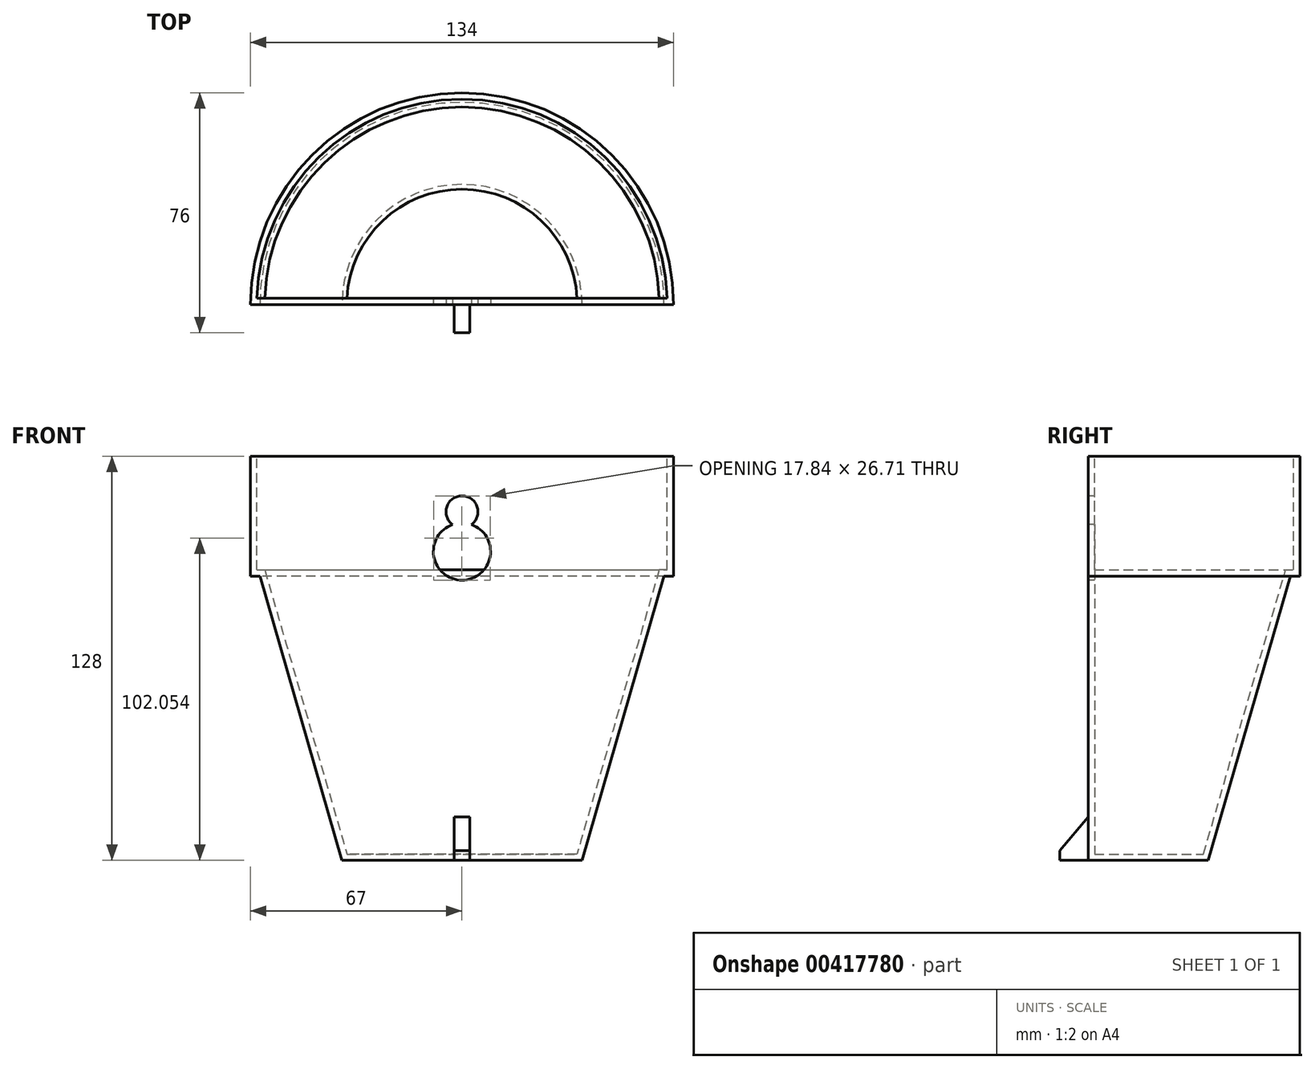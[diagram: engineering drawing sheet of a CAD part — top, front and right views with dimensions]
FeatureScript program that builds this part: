
annotation { "Feature Type Name" : "Feature", "Feature Type Description" : "" }
export const myFeature = defineFeature(function(context is Context, id is Id, definition is map)
    precondition{}
    {
        {
            var Q0;
            Q0=qCreatedBy(makeId("Front.planeOp"),FACE);
            var sketch = newSketch(context, id + "F0", { "sketchPlane" : qUnion([Q0])});
            skLineSegment(sketch, "E0", {"start": v(0, 56.42) * mm, "end": v(-67, 56.42) * mm});
            skLineSegment(sketch, "E1", {"start": v(-67, 56.42) * mm, "end": v(-67, 18.42) * mm});
            skLineSegment(sketch, "E2", {"start": v(0, -71.58) * mm, "end": v(-38, -71.58) * mm});
            skLineSegment(sketch, "E3", {"start": v(-67, 18.42) * mm, "end": v(-64, 18.42) * mm});
            skLineSegment(sketch, "E4", {"start": v(0, 56.42) * mm, "end": v(0, -71.58) * mm});
            skLineSegment(sketch, "E5", {"start": v(-64, 18.42) * mm, "end": v(-38, -71.58) * mm});
            skLineSegment(sketch, "E6.MirrorCS", {"start": v(0, 56.42) * mm, "end": v(67, 56.42) * mm});
            skLineSegment(sketch, "E7.MirrorCS", {"start": v(67, 56.42) * mm, "end": v(67, 18.42) * mm});
            skLineSegment(sketch, "E8.MirrorCS", {"start": v(67, 18.42) * mm, "end": v(64, 18.42) * mm});
            skLineSegment(sketch, "E9.MirrorCS", {"start": v(64, 18.42) * mm, "end": v(38, -71.58) * mm});
            skLineSegment(sketch, "E10.MirrorCS", {"start": v(0, -71.58) * mm, "end": v(38, -71.58) * mm});
            skSolve(sketch);
        }
        {
            var Q0;
            {var subQ0=sQuery(id+"F0.wireOp",EDGE,"E3");Q0=makeQuery(id+"F0.imprint","IMPRINT",FACE,{"disambiguationData":[TD([[makeQuery(id+"F0.imprint","IMPRINT",EDGE,{"derivedFrom":subQ0}),1.0]])]});}
            var Q1;
            {var subQ1=sQuery(id+"F0.wireOp",EDGE,"E0");Q1=makeQuery(id+"F0.imprint","IMPRINT",FACE,{"disambiguationData":[TD([[makeQuery(id+"F0.imprint","IMPRINT",EDGE,{"derivedFrom":subQ1}),1.0]])]});}
            var Q2;
            Q2=makeQuery(id+"F0.imprint","IMPRINT",FACE,{"disambiguationData":[TD([[makeQuery(id+"F0.imprint","IMPRINT",EDGE,{"derivedFrom":sQuery(id+"F0.wireOp",EDGE,"Kfnrekvc-ZjTY-c2iQ-cK4z-hKnBe4uEAVNk")}),1.0]])]});
            var Q3;
            Q3=sQuery(id+"F0.wireOp",EDGE,"E4");
            revolve(context, id + "F1", {"entities" : qUnion([Q0, Q1, Q2]), "axis" : qUnion([Q3]), "revolveType" : RevolveType.ONE_DIRECTION, "angle" : 180 * degree});
        }
        {
            var Q0;
            Q0=makeQuery(id+"FK2OT3XlAi37Aaq_1.splitOp","SPLIT",FACE,{"derivedFrom":makeQuery(id+"F1.opRevolve","SWEPT_FACE",FACE,{"disambiguationData":[OSD([sQuery(id+"F0.wireOp",EDGE,"E0")])]}),"isFromBackBody":true});
            shell(context, id + "F2", {"entities" : qUnion([Q0]), "thickness" : 2 * mm});
        }
        {
            var Q0;
            Q0=qCreatedBy(makeId("Front.planeOp"),FACE);
            var sketch = newSketch(context, id + "F3", { "sketchPlane" : qUnion([Q0])});
            skLineSegment(sketch, "E11.bottom", {"start": v(-2.5, -56.58) * mm, "end": v(2.5, -56.58) * mm});
            skLineSegment(sketch, "E11.top", {"start": v(-2.5, -71.58) * mm, "end": v(2.5, -71.58) * mm});
            skLineSegment(sketch, "E11.left", {"start": v(-2.5, -56.58) * mm, "end": v(-2.5, -71.58) * mm});
            skLineSegment(sketch, "E11.right", {"start": v(2.5, -56.58) * mm, "end": v(2.5, -71.58) * mm});
            skPoint(sketch, "E11.middle", {"position": v(0, -64.08) * mm});
            skSolve(sketch);
        }
        {
            var Q0;
            Q0=qSketchRegion(id+"F3",true);
            extrude(context, id + "F4", {"entities" : qUnion([Q0]), "operationType" : NewBodyOperationType.ADD, "depth" : 9 * mm});
        }
        {
            var Q0;
            Q0=qCreatedBy(makeId("Front.planeOp"),FACE);
            var sketch = newSketch(context, id + "F5", { "sketchPlane" : qUnion([Q0])});
            skCircle(sketch, "E12", {"center": v(0, 38.78) * mm, "radius": 5.05 * mm});
            skCircle(sketch, "E13", {"center": v(0, 26.17) * mm, "radius": 9.05 * mm});
            skSolve(sketch);
        }
        {
            var Q0;
            {var subQ0=sQuery(id+"F5.wireOp",EDGE,"E13");var subQ1=sQuery(id+"F5.wireOp",EDGE,"E12");var subQ2=makeQuery(id+"F5.imprint","INTERSECT",VERTEX,{"disambiguationData":[OD(0.0)],"derivedFrom":[subQ1,subQ0]});Q0=makeQuery(id+"F5.imprint","IMPRINT",FACE,{"disambiguationData":[TD([[makeQuery(id+"F5.imprint","IMPRINT",EDGE,{"disambiguationData":[TD([[subQ2,1.0]])],"derivedFrom":subQ1}),1.0]])]});}
            var Q1;
            {var subQ0=sQuery(id+"F5.wireOp",EDGE,"E13");var subQ1=sQuery(id+"F5.wireOp",EDGE,"E12");var subQ2=makeQuery(id+"F5.imprint","INTERSECT",VERTEX,{"disambiguationData":[OD(0.0)],"derivedFrom":[subQ1,subQ0]});Q1=makeQuery(id+"F5.imprint","IMPRINT",FACE,{"disambiguationData":[TD([[makeQuery(id+"F5.imprint","IMPRINT",EDGE,{"disambiguationData":[TD([[subQ2,-1.0]])],"derivedFrom":subQ1}),-1.0]])]});}
            var Q2;
            {var subQ0=sQuery(id+"F5.wireOp",EDGE,"E13");var subQ1=sQuery(id+"F5.wireOp",EDGE,"E12");var subQ2=makeQuery(id+"F5.imprint","INTERSECT",VERTEX,{"disambiguationData":[OD(0.0)],"derivedFrom":[subQ1,subQ0]});Q2=makeQuery(id+"F5.imprint","IMPRINT",FACE,{"disambiguationData":[TD([[makeQuery(id+"F5.imprint","IMPRINT",EDGE,{"disambiguationData":[TD([[subQ2,-1.0]])],"derivedFrom":subQ1}),1.0]])]});}
            var Q3;
            Q3=sQuery(id+"F5.wireOp",EDGE,"E12");
            var Q4;
            Q4=sQuery(id+"F5.wireOp",EDGE,"E13");
            extrude(context, id + "F6", {"entities" : qUnion([Q0, Q1, Q2]), "operationType" : NewBodyOperationType.REMOVE, "surfaceEntities" : qUnion([Q3, Q4]), "oppositeDirection" : true, "depth" : 10 * mm});
        }
        {
            var Q0;
            Q0=makeQuery(id+"F4.opExtrude","CAP_EDGE",EDGE,{"disambiguationData":[OSD([sQuery(id+"F3.wireOp",EDGE,"E11.bottom")])],"isStart":false});
            chamfer(context, id + "F7", {"entities" : qUnion([Q0]), "chamferType" : ChamferType.OFFSET_ANGLE, "width" : 10 * mm, "oppositeDirection" : false, "angle" : 50 * degree, "tangentPropagation" : true});
        }
    });
